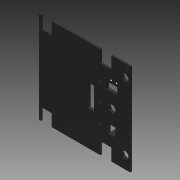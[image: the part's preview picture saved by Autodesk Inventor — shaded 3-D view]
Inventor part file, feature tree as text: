
AUTODESK INVENTOR PART (.ipt)
format: ipt  version: 2015 (Build 190159000, 159)  size: 309,760 bytes
history: native  units: mm
features: sketch x15, extrude x12
ambient origin geometry x8: Origin, YZ Plane, XZ Plane, XY Plane, X Axis, Y Axis, Z Axis, Center Point
bodies: Solid1 (feature_tree)
feature tree (27):
  extrude  "Extrusion1"  Depth=22.5mm
  extrude  "Extrusion2"  Depth=22.5mm
  extrude  "Extrusion3"  Depth=170.0mm
  sketch  "Sketch5"  dims[d7=170.0mm d8=20.0mm]
  extrude  "Extrusion4"  Depth=20.0mm
  extrude  "Extrusion5"  Depth=4.0mm
  sketch  "Sketch8"  dims[d14=4.5mm d15=2.5mm]
  extrude  "Extrusion6"  Depth=6.5mm
  sketch  "Sketch10"  dims[d19=4.5mm d20=2.5mm]
  extrude  "Extrusion7"  Depth=2.5mm
  extrude  "Extrusion8"  Depth=6.5mm
  extrude  "Extrusion9"  Depth=2.5mm
  extrude  "Extrusion10"  Depth=2.0mm TaperAngle=0.0deg
  extrude  "Extrusion11"  Depth=5.5mm
  extrude  "Extrusion12"  Depth=3.0mm
  sketch  "Sketch1"  dims[d0=35.5mm d2=22.5mm]
  sketch  "Sketch2"  dims[d3=22.5mm d4=22.5mm]
  sketch  "Sketch3"  dims[d5=22.5mm d6=170.0mm]
  sketch  "Sketch6"  dims[d9=20.0mm d10=4.0mm]
  sketch  "Sketch7"  dims[d11=3.0mm d12=0.0mm d13=6.5mm]
  sketch  "Sketch9"  dims[d17=4.5mm d18=6.5mm]
  sketch  "Sketch11"  dims[d21=2.5mm d24=2.0mm d25=0.0mm]
  sketch  "Sketch12"  dims[d26=5.5mm d27=5.5mm]
  sketch  "Sketch13"  dims[d28=3.0mm d29=3.0mm]
  sketch  "Sketch14"  dims[d30=3.0mm]
  sketch  "Sketch15"  dims[d32=90.0mm]
  sketch  "Sketch16"  dims[d33=90.0mm d34=4.0mm d36=3.0mm d37=5.5mm d38=3.0mm d39=3.0mm d40=5.0mm d41=0.0mm d42=22.5mm d43=22.5mm d44=22.5mm d48=5.5mm d49=136.0mm d52=165.0mm d54=14.5mm d55=13.5mm d56=13.5mm d57=5.0mm d58=0.0mm d59=25.0mm d61=13.5mm d62=5.0mm d63=0.0mm d64=20.0mm d65=2.0mm d66=10.0mm d67=0.0mm d68=2.0mm d69=6.0mm d70=3.0mm d71=2.0mm d72=0.0mm d74=6.8mm d75=16.0mm d76=13.6mm d77=5.0mm d78=0.0mm d79=20.0mm d80=10.0mm d81=13.0mm d82=20.0mm d83=5.0mm d84=0.0mm d85=2.0mm d86=2.0mm d87=15.0mm d88=0.0mm d90=5.0mm d91=5.0mm d92=5.0mm d93=5.0mm d94=0.0mm d97=41.5mm d98=11.2mm d99=65.0mm d100=64.25mm d101=64.25mm d102=3.0mm d103=3.0mm d104=3.0mm d105=3.0mm d106=5.5mm d107=5.5mm d108=5.7mm d109=5.7mm d110=10.0mm d111=0.0mm d112=6.5mm d113=6.5mm d114=4.5mm d115=4.0mm d116=4.5mm d117=4.5mm d118=14.5mm d120=12.0mm d121=12.0mm]
